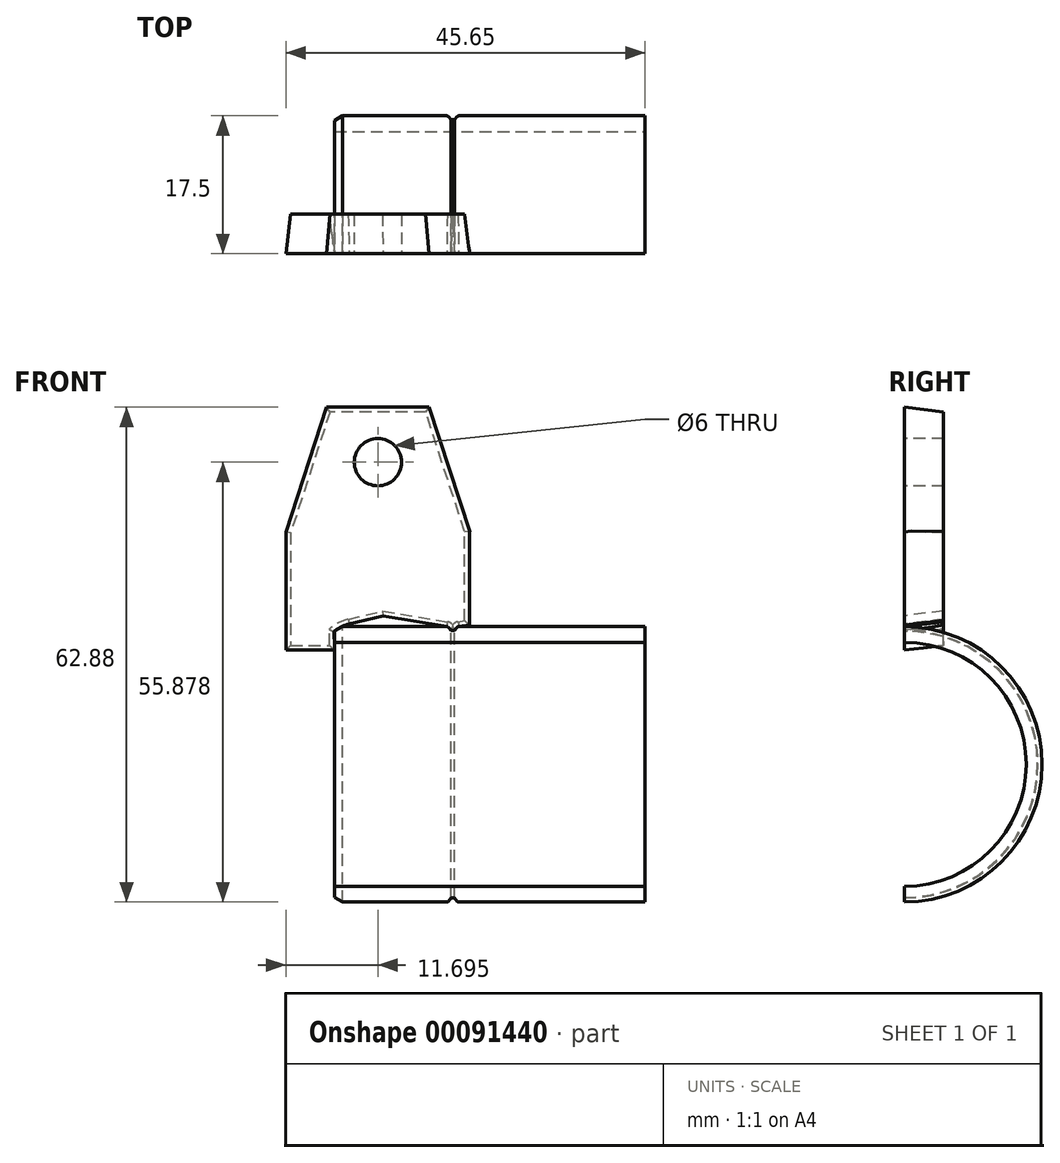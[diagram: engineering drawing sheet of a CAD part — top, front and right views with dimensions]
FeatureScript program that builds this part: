
annotation { "Feature Type Name" : "Feature", "Feature Type Description" : "" }
export const myFeature = defineFeature(function(context is Context, id is Id, definition is map)
    precondition{}
    {
        {
            var Q0;
            Q0=qCreatedBy(makeId("Front.planeOp"),FACE);
            var sketch = newSketch(context, id + "F0", { "sketchPlane" : qUnion([Q0])});
            skLineSegment(sketch, "E0", {"start": v(1, 0.04) * mm, "end": v(14.25, 0.04) * mm});
            skLineSegment(sketch, "E1", {"start": v(0, -0.53) * mm, "end": v(0, -1.96) * mm});
            skArc(sketch, "E2.filletArc", {"start": v(14.44, -0.04) * mm, "mid": v(14.35, 0.02) * mm, "end": v(14.25, 0.04) * mm});
            skArc(sketch, "E3.MirrorCS", {"start": v(15.56, -0.04) * mm, "mid": v(15.65, 0.02) * mm, "end": v(15.75, 0.04) * mm});
            skLineSegment(sketch, "E4", {"start": v(0, -1.96) * mm, "end": v(19.04, -1.96) * mm});
            skLineSegment(sketch, "E5", {"start": v(15.75, 0.04) * mm, "end": v(18.88, 0.04) * mm});
            skLineSegment(sketch, "E6", {"start": v(18.88, 0.04) * mm, "end": v(39.45, 0.04) * mm});
            skLineSegment(sketch, "E7", {"start": v(39.45, 0.04) * mm, "end": v(39.45, -1.96) * mm});
            skLineSegment(sketch, "E8", {"start": v(39.45, -1.96) * mm, "end": v(19.04, -1.96) * mm});
            skLineSegment(sketch, "E9", {"start": v(0, -0.53) * mm, "end": v(1, 0.04) * mm});
            skLineSegment(sketch, "E10", {"start": v(14.8, -0.46) * mm, "end": v(15.2, -0.46) * mm});
            skLineSegment(sketch, "E11", {"start": v(14.44, -0.04) * mm, "end": v(14.8, -0.46) * mm});
            skLineSegment(sketch, "E12", {"start": v(15.2, -0.46) * mm, "end": v(15.56, -0.04) * mm});
            skSolve(sketch);
        }
        {
            var Q0;
            Q0=qCreatedBy(makeId("Front.planeOp"),FACE);
            var sketch = newSketch(context, id + "F1", { "sketchPlane" : qUnion([Q0])});
            skLineSegment(sketch, "E13", {"start": v(0.33, -17.46) * mm, "end": v(58.88, -17.46) * mm});
            skSolve(sketch);
        }
        {
            var Q0;
            Q0 = qSketchRegion(id + "F0", true);
            var Q1;
            Q1=sQuery(id+"F1.wireOp",EDGE,"E13");
            revolve(context, id + "F2", {"entities" : qUnion([Q0]), "axis" : qUnion([Q1]), "revolveType" : RevolveType.ONE_DIRECTION, "oppositeDirection" : true, "angle" : 180 * degree});
        }
        {
            var Q0;
            Q0=qCreatedBy(makeId("Front.planeOp"),FACE);
            var sketch = newSketch(context, id + "F3", { "sketchPlane" : qUnion([Q0])});
            skLineSegment(sketch, "E14", {"start": v(-0.3, -2.95) * mm, "end": v(-6.2, -2.95) * mm});
            skLineSegment(sketch, "E15", {"start": v(0, -2.64) * mm, "end": v(-0.07, -0.6) * mm});
            skArc(sketch, "E16.filletArc", {"start": v(-0.3, -2.95) * mm, "mid": v(-0.08, -2.86) * mm, "end": v(0, -2.64) * mm});
            skLineSegment(sketch, "E17", {"start": v(14.85, -0.46) * mm, "end": v(15.15, -0.46) * mm});
            skLineSegment(sketch, "E18", {"start": v(15.75, 0.04) * mm, "end": v(17.12, 0.26) * mm});
            skLineSegment(sketch, "E19", {"start": v(17.12, 0.26) * mm, "end": v(17.12, 12.05) * mm});
            skLineSegment(sketch, "E20", {"start": v(17.17, 12.05) * mm, "end": v(12.01, 27.92) * mm});
            skLineSegment(sketch, "E21", {"start": v(-6.2, -2.95) * mm, "end": v(-6.2, 12.05) * mm});
            skLineSegment(sketch, "E22", {"start": v(-6.2, 12.05) * mm, "end": v(-1.05, 27.92) * mm});
            skLineSegment(sketch, "E23", {"start": v(-1.05, 27.92) * mm, "end": v(12.01, 27.92) * mm});
            skArc(sketch, "E24", {"start": v(1.86, 0.35) * mm, "mid": v(0.84, 0) * mm, "end": v(-0.07, -0.6) * mm});
            skLineSegment(sketch, "E25", {"start": v(1.86, 0.35) * mm, "end": v(6.12, 1.4) * mm});
            skLineSegment(sketch, "E26", {"start": v(-6.2, 12.05) * mm, "end": v(17.17, 12.05) * mm});
            skArc(sketch, "E27.MirrorCS", {"start": v(15.56, -0.04) * mm, "mid": v(15.65, 0.02) * mm, "end": v(15.75, 0.04) * mm});
            skLineSegment(sketch, "E28", {"start": v(15.23, -0.42) * mm, "end": v(15.56, -0.04) * mm});
            skArc(sketch, "E29.MirrorCS", {"start": v(14.44, -0.04) * mm, "mid": v(14.35, 0.02) * mm, "end": v(14.25, 0.04) * mm});
            skLineSegment(sketch, "E30.MirrorCS", {"start": v(14.77, -0.42) * mm, "end": v(14.44, -0.04) * mm});
            skLineSegment(sketch, "E31", {"start": v(6.12, 1.4) * mm, "end": v(14.25, 0.04) * mm});
            skPoint(sketch, "E32.visualSharp", {"position": v(14.8, -0.46) * mm});
            skArc(sketch, "E32.filletArc", {"start": v(14.77, -0.42) * mm, "mid": v(14.8, -0.45) * mm, "end": v(14.85, -0.46) * mm});
            skPoint(sketch, "E33.visualSharp", {"position": v(15.2, -0.46) * mm});
            skArc(sketch, "E33.filletArc", {"start": v(15.15, -0.46) * mm, "mid": v(15.2, -0.45) * mm, "end": v(15.23, -0.42) * mm});
            skSolve(sketch);
        }
        {
            var Q0;
            Q0 = qSketchRegion(id + "F3", true);
            extrude(context, id + "F4", {"entities" : qUnion([Q0]), "oppositeDirection" : true, "depth" : 5 * mm, "hasDraft" : true, "draftAngle" : 7 * degree, "draftPullDirection" : true});
        }
        {
            var Q0;
            {var subQ3=sQuery(id+"F3.wireOp",EDGE,"E20");Q0=makeQuery(id+"F3.imprint","IMPRINT",FACE,{"disambiguationData":[TD([[makeQuery(id+"F3.imprint","IMPRINT",EDGE,{"derivedFrom":subQ3}),1.0]])]});}
            var sketch = newSketch(context, id + "F5", { "sketchPlane" : qUnion([Q0])});
            skCircle(sketch, "E34", {"center": v(5.5, 20.92) * mm, "radius": 3 * mm});
            skSolve(sketch);
        }
        {
            var Q0;
            Q0 = qSketchRegion(id + "F5", true);
            extrude(context, id + "F6", {"entities" : qUnion([Q0]), "operationType" : NewBodyOperationType.REMOVE, "oppositeDirection" : true, "depth" : 7 * mm});
        }
    });
